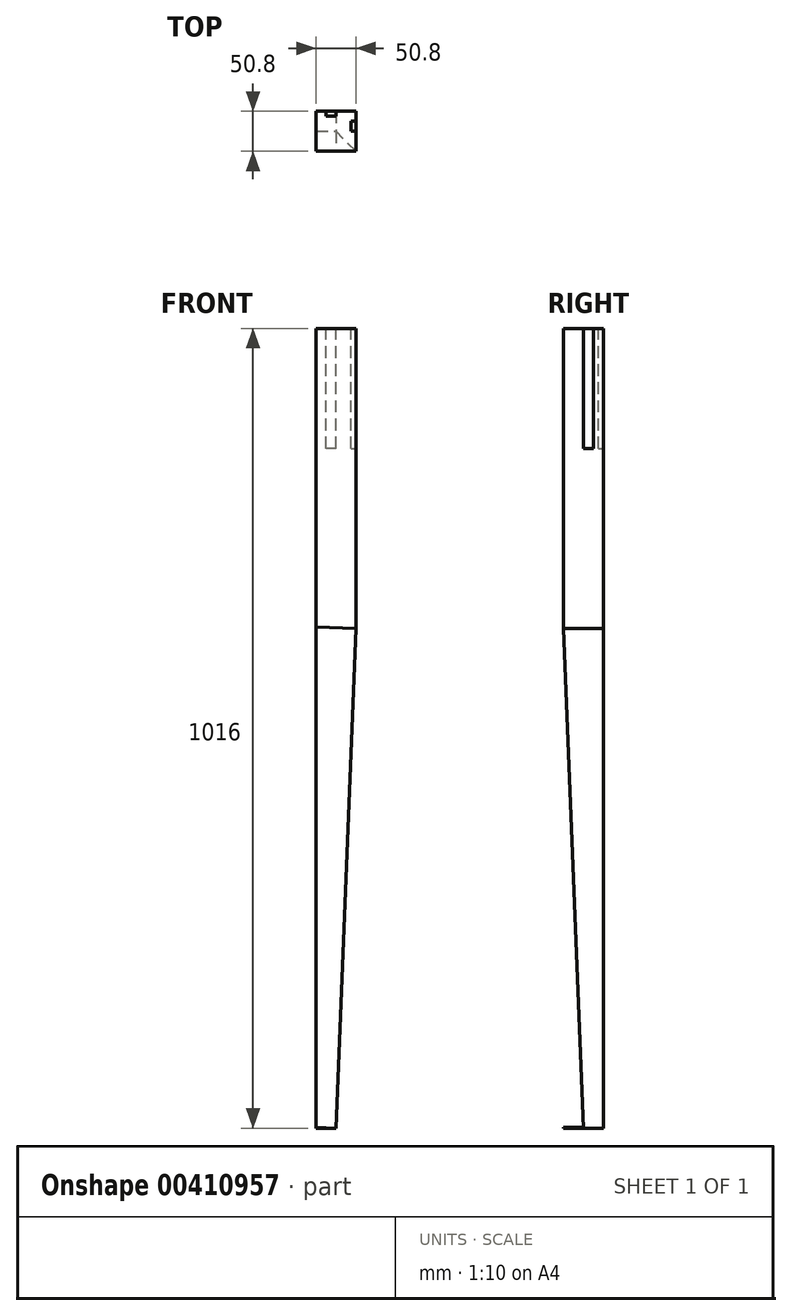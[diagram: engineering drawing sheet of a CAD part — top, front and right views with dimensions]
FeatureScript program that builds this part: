
annotation { "Feature Type Name" : "Feature", "Feature Type Description" : "" }
export const myFeature = defineFeature(function(context is Context, id is Id, definition is map)
    precondition{}
    {
        {
            var Q0;
            Q0=qCreatedBy(makeId("Front.planeOp"),FACE);
            var sketch = newSketch(context, id + "F0", { "sketchPlane" : qUnion([Q0])});
            skLineSegment(sketch, "E0", {"start": v(0, -1016) * mm, "end": v(0, 0) * mm});
            skLineSegment(sketch, "E1", {"start": v(0, 0) * mm, "end": v(50.8, 0) * mm});
            skLineSegment(sketch, "E2", {"start": v(50.8, 0) * mm, "end": v(50.8, -381) * mm});
            skLineSegment(sketch, "E3", {"start": v(50.8, -381) * mm, "end": v(25.4, -1016) * mm});
            skLineSegment(sketch, "E4", {"start": v(25.4, -1016) * mm, "end": v(0, -1016) * mm});
            skSolve(sketch);
        }
        {
            var Q0;
            Q0 = qSketchRegion(id + "F0", true);
            extrude(context, id + "F1", {"entities" : qUnion([Q0]), "oppositeDirection" : true, "depth" : 50.8 * mm});
        }
        {
            var Q0;
            Q0=makeQuery(id+"F1.opExtrude","SWEPT_FACE",FACE,{"disambiguationData":[OSD([sQuery(id+"F0.wireOp",EDGE,"E2")])]});
            var sketch = newSketch(context, id + "F2", { "sketchPlane" : qUnion([Q0])});
            skLineSegment(sketch, "E5.bottom", {"start": v(38.1, -152.4) * mm, "end": v(25.4, -152.4) * mm});
            skLineSegment(sketch, "E5.top", {"start": v(38.1, 0) * mm, "end": v(25.4, 0) * mm});
            skLineSegment(sketch, "E5.left", {"start": v(38.1, -152.4) * mm, "end": v(38.1, 0) * mm});
            skLineSegment(sketch, "E5.right", {"start": v(25.4, -152.4) * mm, "end": v(25.4, 0) * mm});
            skSolve(sketch);
        }
        {
            var Q0;
            Q0 = qSketchRegion(id + "F2", true);
            extrude(context, id + "F3", {"entities" : qUnion([Q0]), "operationType" : NewBodyOperationType.REMOVE, "oppositeDirection" : true, "depth" : 6.35 * mm});
        }
        {
            var Q0;
            Q0=makeQuery(id+"F1.opExtrude","SWEPT_FACE",FACE,{"disambiguationData":[OSD([sQuery(id+"F0.wireOp",EDGE,"E3")])]});
            var sketch = newSketch(context, id + "F4", { "sketchPlane" : qUnion([Q0])});
            skLineSegment(sketch, "E6", {"start": v(0, -378.67) * mm, "end": v(25.4, -1014.17) * mm});
            skLineSegment(sketch, "E7", {"start": v(25.4, -1014.17) * mm, "end": v(0, -1014.17) * mm});
            skLineSegment(sketch, "E8", {"start": v(0, -1014.17) * mm, "end": v(0, -378.67) * mm});
            skSolve(sketch);
        }
        {
            var Q0;
            Q0=makeQuery(id+"F4.imprint","IMPRINT",FACE,{"disambiguationData":[TD([[makeQuery(id+"F4.imprint","IMPRINT",EDGE,{"derivedFrom":sQuery(id+"F4.wireOp",EDGE,"E6")}),-1.0]])]});
            var Q1;
            Q1=sQuery(id+"F4.wireOp",EDGE,"E8");
            var Q2;
            Q2=sQuery(id+"F4.wireOp",EDGE,"E6");
            var Q3;
            Q3=sQuery(id+"F4.wireOp",EDGE,"E7");
            extrude(context, id + "F5", {"entities" : qUnion([Q0]), "operationType" : NewBodyOperationType.REMOVE, "surfaceEntities" : qUnion([Q1, Q2, Q3]), "endBound" : BoundingType.THROUGH_ALL, "oppositeDirection" : true, "depth" : 25.4 * mm});
        }
        {
            var Q0;
            Q0=makeQuery(id+"F1.opExtrude","CAP_FACE",FACE,{"disambiguationData":[OSD([sQuery(id+"F0.wireOp",EDGE,"E0"),sQuery(id+"F0.wireOp",EDGE,"E1"),sQuery(id+"F0.wireOp",EDGE,"E2"),sQuery(id+"F0.wireOp",EDGE,"E3"),sQuery(id+"F0.wireOp",EDGE,"E4")])],"isStart":false});
            var sketch = newSketch(context, id + "F6", { "sketchPlane" : qUnion([Q0])});
            skPoint(sketch, "E9.firstSnap0", {"position": v(-25.4, 0) * mm});
            skLineSegment(sketch, "E9.bottom", {"start": v(-25.4, -152.4) * mm, "end": v(-12.7, -152.4) * mm});
            skLineSegment(sketch, "E9.top", {"start": v(-25.4, 0) * mm, "end": v(-12.7, 0) * mm});
            skLineSegment(sketch, "E9.left", {"start": v(-25.4, -152.4) * mm, "end": v(-25.4, 0) * mm});
            skLineSegment(sketch, "E9.right", {"start": v(-12.7, -152.4) * mm, "end": v(-12.7, 0) * mm});
            skSolve(sketch);
        }
        {
            var Q0;
            Q0 = qSketchRegion(id + "F6", true);
            extrude(context, id + "F7", {"entities" : qUnion([Q0]), "operationType" : NewBodyOperationType.REMOVE, "oppositeDirection" : true, "depth" : 6.35 * mm});
        }
    });
